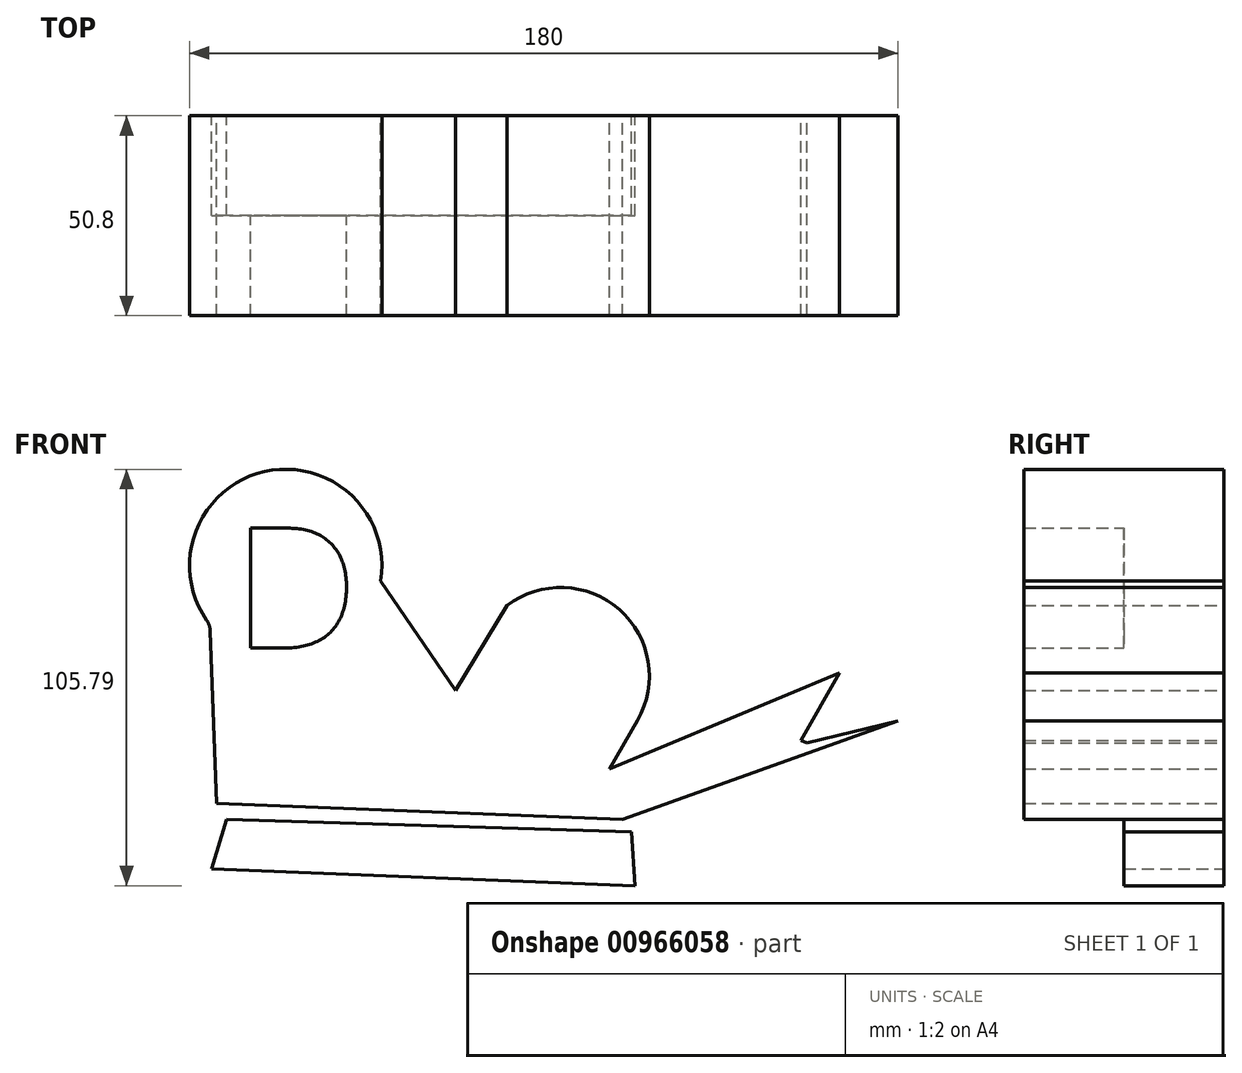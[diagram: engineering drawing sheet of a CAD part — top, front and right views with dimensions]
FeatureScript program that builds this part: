
annotation { "Feature Type Name" : "Feature", "Feature Type Description" : "" }
export const myFeature = defineFeature(function(context is Context, id is Id, definition is map)
    precondition{}
    {
        {
            var Q0;
            Q0=qCreatedBy(makeId("Front.planeOp"),FACE);
            var sketch = newSketch(context, id + "F0", { "sketchPlane" : qUnion([Q0])});
            skArc(sketch, "E0", {"start": v(-7.78, 27.8) * mm, "mid": v(-37.98, 55.41) * mm, "end": v(-51.1, 16.65) * mm});
            skLineSegment(sketch, "E1", {"start": v(-7.78, 27.8) * mm, "end": v(11.32, 0) * mm});
            skLineSegment(sketch, "E2", {"start": v(11.32, 0) * mm, "end": v(24.36, 21.55) * mm});
            skArc(sketch, "E3", {"start": v(57.5, -7.58) * mm, "mid": v(52.87, 20.56) * mm, "end": v(24.36, 21.55) * mm});
            skLineSegment(sketch, "E4", {"start": v(57.5, -7.58) * mm, "end": v(43.24, -32.32) * mm});
            skLineSegment(sketch, "E5", {"start": v(50.37, -19.95) * mm, "end": v(108.84, 4.42) * mm});
            skLineSegment(sketch, "E6", {"start": v(108.84, 4.42) * mm, "end": v(98.98, -12.67) * mm});
            skLineSegment(sketch, "E7", {"start": v(100.53, -13.35) * mm, "end": v(123.67, -7.73) * mm});
            skLineSegment(sketch, "E8", {"start": v(123.67, -7.73) * mm, "end": v(53.66, -32.73) * mm});
            skLineSegment(sketch, "E9", {"start": v(53.66, -32.73) * mm, "end": v(43.24, -32.32) * mm});
            skLineSegment(sketch, "E10", {"start": v(98.98, -12.67) * mm, "end": v(100.53, -13.35) * mm});
            skLineSegment(sketch, "E11", {"start": v(43.24, -32.32) * mm, "end": v(-49.42, -28.72) * mm});
            skLineSegment(sketch, "E12", {"start": v(-49.42, -28.72) * mm, "end": v(-51.1, 16.65) * mm});
            skLineSegment(sketch, "E13", {"start": v(-49.42, -28.72) * mm, "end": v(53.66, -51.3) * mm});
            skLineSegment(sketch, "E14", {"start": v(53.66, -51.3) * mm, "end": v(53.66, -38.87) * mm});
            skLineSegment(sketch, "E15", {"start": v(53.66, -32.73) * mm, "end": v(53.66, -38.87) * mm});
            skSolve(sketch);
        }
        {
            var Q0;
            {var subQ0=sQuery(id+"F0.wireOp",EDGE,"E5");Q0=makeQuery(id+"F0.imprint","IMPRINT",FACE,{"disambiguationData":[TD([[makeQuery(id+"F0.imprint","IMPRINT",EDGE,{"derivedFrom":subQ0}),-1.0]])]});}
            var Q1;
            Q1=makeQuery(id+"F0.imprint","IMPRINT",FACE,{"disambiguationData":[TD([[makeQuery(id+"F0.imprint","IMPRINT",EDGE,{"derivedFrom":sQuery(id+"F0.wireOp",EDGE,"E0")}),1.0]])]});
            extrude(context, id + "F1", {"entities" : qUnion([Q0, Q1]), "depth" : 25.4 * mm, "offsetDistance" : 25.4 * mm});
        }
        {
            var Q0;
            Q0=qCreatedBy(makeId("Front.planeOp"),FACE);
            var sketch = newSketch(context, id + "F2", { "sketchPlane" : qUnion([Q0])});
            skLineSegment(sketch, "E16", {"start": v(-46.87, -32.82) * mm, "end": v(-50.75, -45.37) * mm});
            skLineSegment(sketch, "E17", {"start": v(-50.75, -45.37) * mm, "end": v(56.8, -49.61) * mm});
            skLineSegment(sketch, "E18", {"start": v(55.98, -35.95) * mm, "end": v(56.8, -49.61) * mm});
            skLineSegment(sketch, "E19", {"start": v(55.98, -35.95) * mm, "end": v(-46.87, -32.82) * mm});
            skSolve(sketch);
        }
        {
            var Q0;
            Q0=makeQuery(id+"F2.imprint","IMPRINT",FACE,{"disambiguationData":[TD([[makeQuery(id+"F2.imprint","IMPRINT",EDGE,{"derivedFrom":sQuery(id+"F2.wireOp",EDGE,"E16")}),1.0]])]});
            extrude(context, id + "F3", {"entities" : qUnion([Q0]), "depth" : 25.4 * mm, "offsetDistance" : 25.4 * mm});
        }
        {
            var Q0;
            Q0=makeQuery(id+"F1.opExtrude","SWEPT_EDGE",EDGE,{"disambiguationData":[OSD([sQuery(id+"F0.wireOp",EDGE,"E0"),sQuery(id+"F0.wireOp",EDGE,"E12")])]});
            fillet(context, id + "F4", {"entities" : qUnion([Q0]), "radius" : 5.08 * mm, "tangentPropagation" : true, "allowEdgeOverflow" : false});
        }
        {
            var Q0;
            Q0=makeQuery(id+"F1.opExtrude","CAP_FACE",FACE,{"disambiguationData":[OSD([sQuery(id+"F0.wireOp",EDGE,"E0"),sQuery(id+"F0.wireOp",EDGE,"E1"),sQuery(id+"F0.wireOp",EDGE,"E2"),sQuery(id+"F0.wireOp",EDGE,"E3"),sQuery(id+"F0.wireOp",EDGE,"E4"),sQuery(id+"F0.wireOp",EDGE,"E5"),sQuery(id+"F0.wireOp",EDGE,"E6"),sQuery(id+"F0.wireOp",EDGE,"E7"),sQuery(id+"F0.wireOp",EDGE,"E8"),sQuery(id+"F0.wireOp",EDGE,"E9"),sQuery(id+"F0.wireOp",EDGE,"E10"),sQuery(id+"F0.wireOp",EDGE,"E11"),sQuery(id+"F0.wireOp",EDGE,"E12")])],"isStart":false});
            var sketch = newSketch(context, id + "F5", { "sketchPlane" : qUnion([Q0])});
            skText(sketch, "E20", { "text": "D", "fontName": "OpenSans-Regular.ttf"});
            skPoint(sketch, "E20.secondSnap0", {"position": v(17.84, 10.78) * mm});
            const initialGuessF5  = {"E20": [-0.04494, 0.01078, 1, 0, 0.03071]};
            skSetInitialGuess(sketch, initialGuessF5);
            skSolve(sketch);
        }
        {
            var Q0;
            Q0=makeQuery(id+"F5.imprint","IMPRINT",FACE,{"disambiguationData":[TD([[makeQuery(id+"F5.imprint","IMPRINT",EDGE,{"derivedFrom":sQuery(id+"F5.wireOp",EDGE,"E20.sketch_text.stroke-0")}),1.0]])]});
            extrude(context, id + "F6", {"entities" : qUnion([Q0]), "operationType" : NewBodyOperationType.ADD, "depth" : 25.4 * mm, "offsetDistance" : 25.4 * mm});
        }
    });
